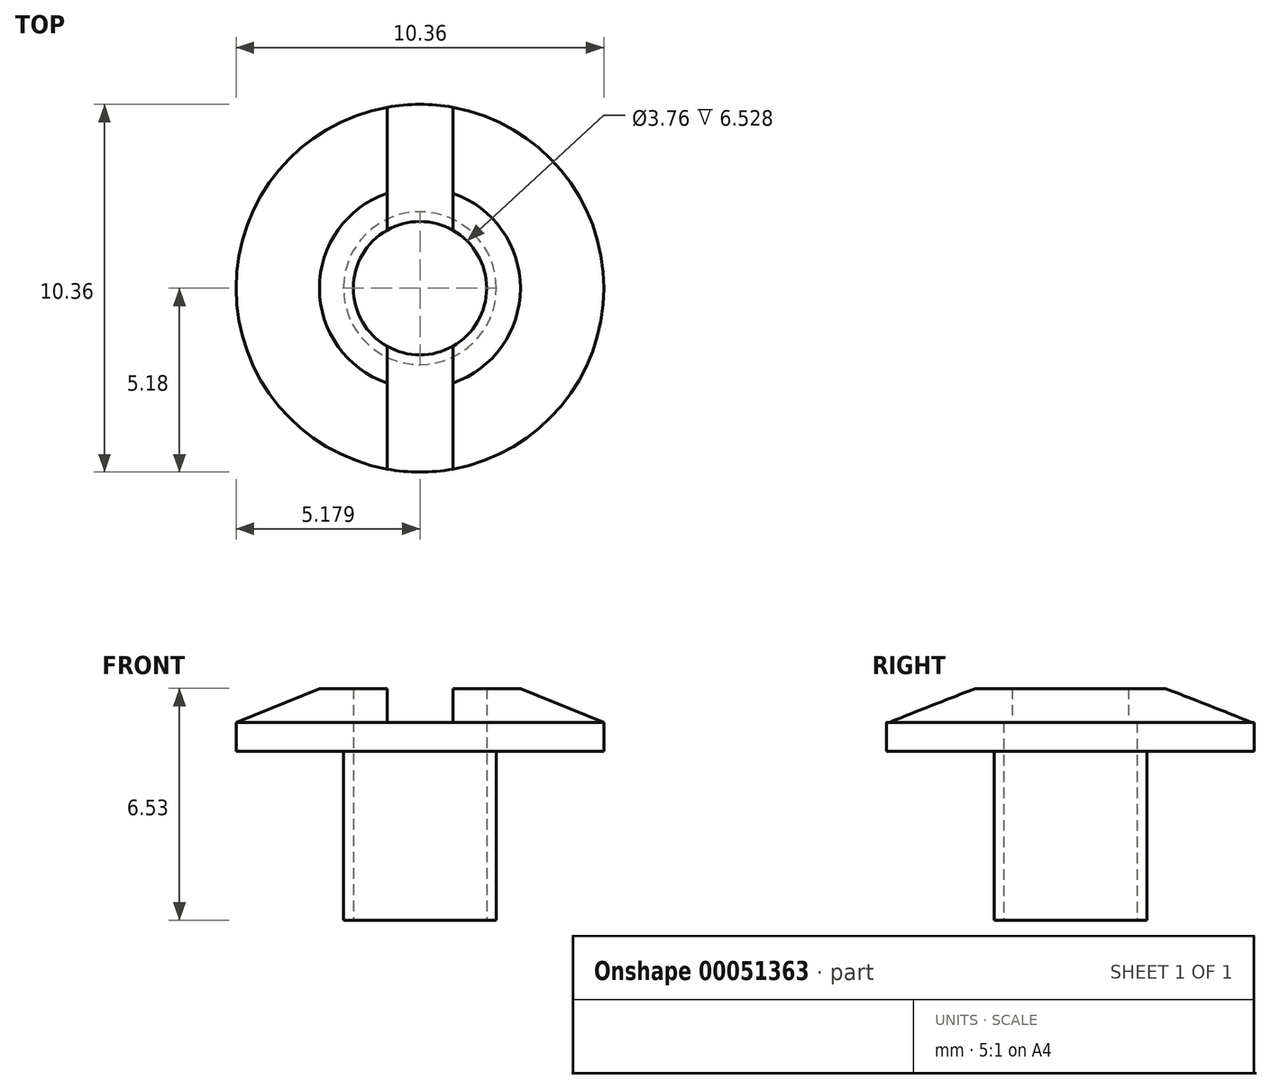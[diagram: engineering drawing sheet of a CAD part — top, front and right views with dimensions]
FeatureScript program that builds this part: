
annotation { "Feature Type Name" : "Feature", "Feature Type Description" : "" }
export const myFeature = defineFeature(function(context is Context, id is Id, definition is map)
    precondition{}
    {
        {
            var Q0;
            Q0=qCreatedBy(makeId("Front.planeOp"),FACE);
            var sketch = newSketch(context, id + "F0", { "sketchPlane" : qUnion([Q0])});
            skLineSegment(sketch, "E0", {"start": v(17.79, 8.88) * mm, "end": v(17.79, 2.35) * mm});
            skLineSegment(sketch, "E1", {"start": v(17.79, 2.35) * mm, "end": v(15.64, 2.35) * mm});
            skLineSegment(sketch, "E2", {"start": v(15.64, 2.35) * mm, "end": v(15.64, 7.11) * mm});
            skLineSegment(sketch, "E3", {"start": v(15.64, 7.11) * mm, "end": v(12.6, 7.11) * mm});
            skLineSegment(sketch, "E4", {"start": v(12.6, 7.11) * mm, "end": v(12.6, 7.93) * mm});
            skLineSegment(sketch, "E5", {"start": v(12.6, 7.93) * mm, "end": v(14.96, 8.88) * mm});
            skLineSegment(sketch, "E6", {"start": v(14.96, 8.88) * mm, "end": v(17.79, 8.88) * mm});
            skSolve(sketch);
        }
        {
            var Q0;
            Q0 = qSketchRegion(id + "F0", true);
            var Q1;
            Q1=sQuery(id+"F0.wireOp",EDGE,"E0");
            revolve(context, id + "F1", {"entities" : qUnion([Q0]), "axis" : qUnion([Q1]), "revolveType" : RevolveType.FULL});
        }
        {
            var Q0;
            Q0=qCreatedBy(makeId("Front.planeOp"),FACE);
            var sketch = newSketch(context, id + "F2", { "sketchPlane" : qUnion([Q0])});
            skLineSegment(sketch, "E7", {"start": v(16.86, 8.88) * mm, "end": v(16.86, 7.93) * mm});
            skLineSegment(sketch, "E8", {"start": v(16.86, 7.93) * mm, "end": v(18.72, 7.93) * mm});
            skLineSegment(sketch, "E9", {"start": v(18.72, 7.93) * mm, "end": v(18.72, 8.88) * mm});
            skLineSegment(sketch, "E10", {"start": v(18.72, 8.88) * mm, "end": v(16.86, 8.88) * mm});
            skPoint(sketch, "E11", {"position": v(17.79, 7.93) * mm});
            skSolve(sketch);
        }
        {
            var Q0;
            Q0 = qSketchRegion(id + "F2", true);
            extrude(context, id + "F3", {"entities" : qUnion([Q0]), "operationType" : NewBodyOperationType.REMOVE, "endBound" : BoundingType.SYMMETRIC, "oppositeDirection" : true, "depth" : 12.7 * mm});
        }
        {
            var Q0;
            Q0=makeQuery(id+"F1.opRevolve","SWEPT_FACE",FACE,{"disambiguationData":[OSD([sQuery(id+"F0.wireOp",EDGE,"E1")])]});
            var sketch = newSketch(context, id + "F4", { "sketchPlane" : qUnion([Q0])});
            skCircle(sketch, "E12", {"center": v(17.79, 0) * mm, "radius": 1.88 * mm});
            skSolve(sketch);
        }
        {
            var Q0;
            Q0 = qSketchRegion(id + "F4", true);
            extrude(context, id + "F5", {"entities" : qUnion([Q0]), "operationType" : NewBodyOperationType.REMOVE, "endBound" : BoundingType.THROUGH_ALL, "oppositeDirection" : true, "depth" : 25.4 * mm});
        }
    });
